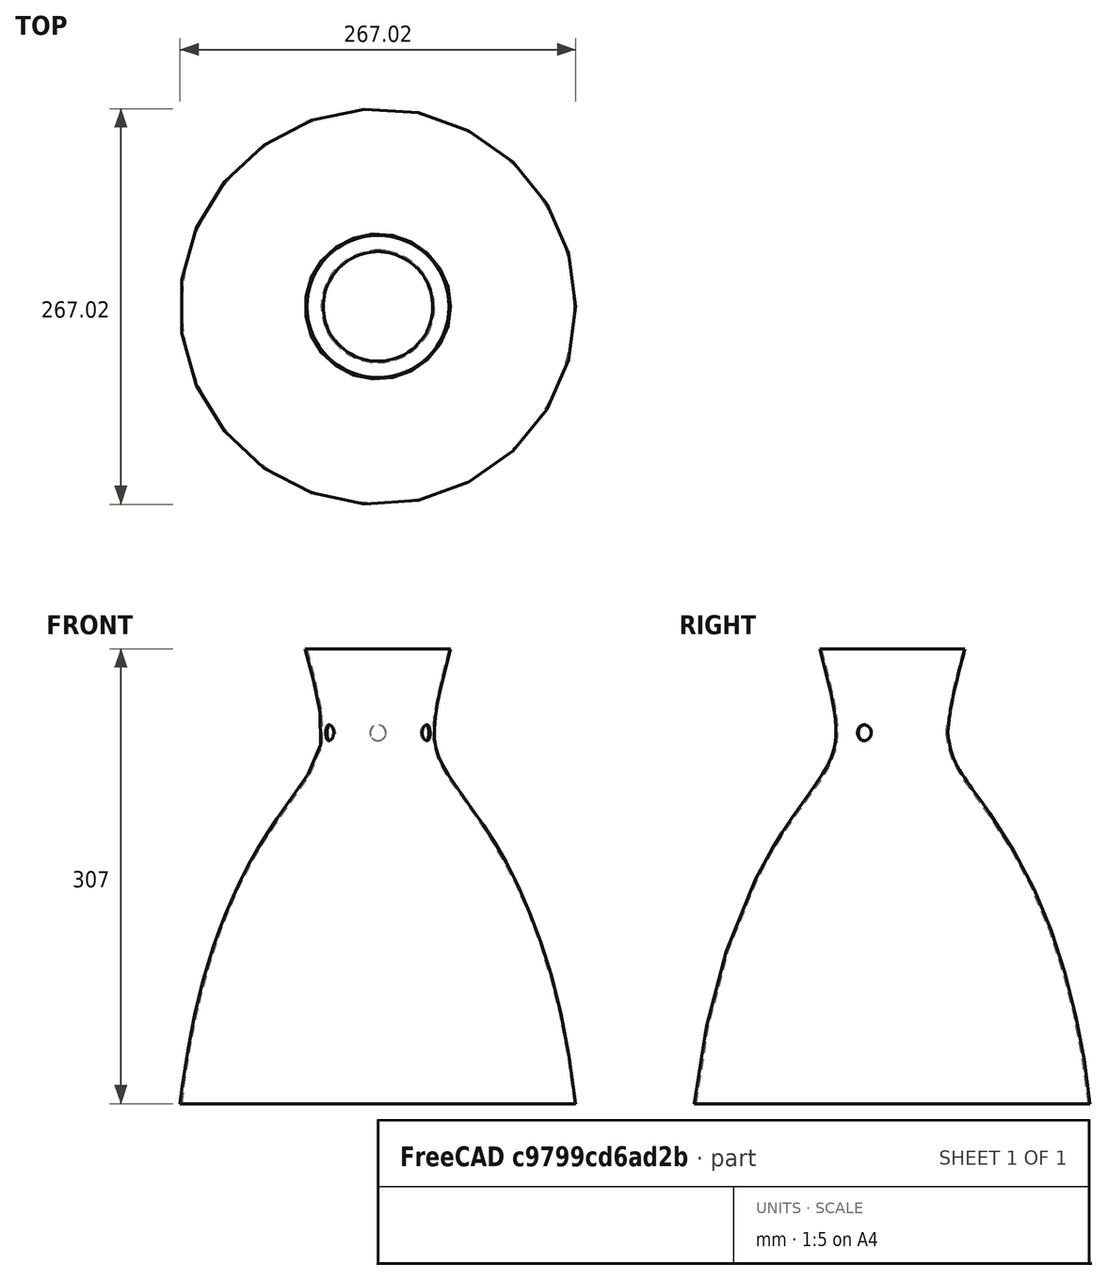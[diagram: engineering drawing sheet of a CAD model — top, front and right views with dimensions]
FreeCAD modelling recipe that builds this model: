
FCSTD DOCUMENT  (FreeCAD 0.20R29603 (Git))
Label: kitchen_lamp_shade_replacement
License: All rights reserved
LicenseURL: http://en.wikipedia.org/wiki/All_rights_reserved
objects: Sketcher::SketchObject×2, PartDesign::Revolution×1, PartDesign::Thickness×1, PartDesign::Pocket×1, PartDesign::PolarPattern×1, PartDesign::Body×1
note: 10 computed .brp shape members not serialized (recipe doc carries the construction recipe); baked Part::Feature solids carry a one-line shape summary decoded from their .brp

FEATURE [Sketcher::SketchObject] Sketch
  FullyConstrained = false
  MapMode = 5
  Placement = pos=(0,0,0) rot=(1,0,0;1.5708rad)
  Support = -> [XZ_Plane]
  sketch-geometry (12):
    g0: LineSegment StartX=0 StartY=0 StartZ=0 EndX=0 EndY=307 EndZ=0
    g1: LineSegment StartX=0 StartY=307 StartZ=0 EndX=48 EndY=307 EndZ=0
    g2: LineSegment StartX=0 StartY=0 StartZ=0 EndX=132.5 EndY=0 EndZ=0
    g3-g7: Circle x5 (B-spline internal-alignment scaffolding for g8; pole/knot coordinates omitted)
    g8: BSplineCurve PolesCount=5 KnotsCount=3 Degree=3 IsPeriodic=0
    g9: GeomPoint X=48 Y=307 Z=0
    g10: GeomPoint X=53.8421 Y=210.771 Z=0
    g11: GeomPoint X=132.5 Y=0 Z=0
  constraints (17):
    c: Coincident(g0,g-1)
    c: PointOnObject(g0,g-2)
    c: Coincident(g1,g0)
    c: Horizontal(g1)
    c: Coincident(g2,g0)
    c: PointOnObject(g2,g-1)
    c: Weight(g3) = 1
    c: Coincident(g8,g1)
    c: Equal(g3, g4-g7) x4
    c: Coincident(g8,g2)
    c: InternalAlignment(g3-g7 -> g8) x5
    c: InternalAlignment(g9,g8)
    c: InternalAlignment(g10,g8)
    c: InternalAlignment(g11,g8)
    c: DistanceY(g0,g0) = 307  'height'
    c: DistanceX(g2,g2) = 132.5  'radius_bottom'
    c: DistanceX(g1,g1) = 48  'radius_top'
FEATURE [PartDesign::Revolution] Revolution
  Angle = 360
  Axis = (0,2e-16,1)
  Base = (0,0,0)
  Placement = pos=(0,0,0) rot=(1,0,0;1.5708rad)
  Profile = -> Sketch
  ReferenceAxis = -> Sketch [V_Axis]
  Reversed = true
FEATURE [Sketcher::SketchObject] Sketch001
  FullyConstrained = false
  MapMode = 5
  Placement = pos=(0,0,0) rot=(1,0,0;1.5708rad)
  Support = -> [XZ_Plane]
  sketch-geometry (1):
    g0: Circle CenterX=0 CenterY=250.338 CenterZ=0 NormalX=0 NormalY=0 NormalZ=1 AngleXU=0 Radius=5.33743
  constraints (1):
    c: PointOnObject(g0,g-2)
FEATURE [PartDesign::Thickness] Thickness
  Base = -> Revolution [Face3,Face1]
  BaseFeature = -> Revolution
  Intersection = false
  Join = 0
  Mode = 0
  SupportTransform = false
  Value = 1
FEATURE [PartDesign::Pocket] Pocket
  BaseFeature = -> Thickness
  Direction = (0,1,2e-16)
  Length = 5
  Length2 = 5
  Profile = -> Sketch001
  ReferenceAxis = -> Sketch001 [N_Axis]
  Type = 1
FEATURE [PartDesign::PolarPattern] PolarPattern
  Angle = 360
  Axis = -> Z_Axis
  BaseFeature = -> Pocket
  Occurrences = 3
  Originals = -> [Pocket]
FEATURE [PartDesign::Body] Body
  Group = -> [Sketch,Revolution,Thickness,Sketch001,Pocket,PolarPattern]
  Origin = -> Origin
  Tip = -> PolarPattern
